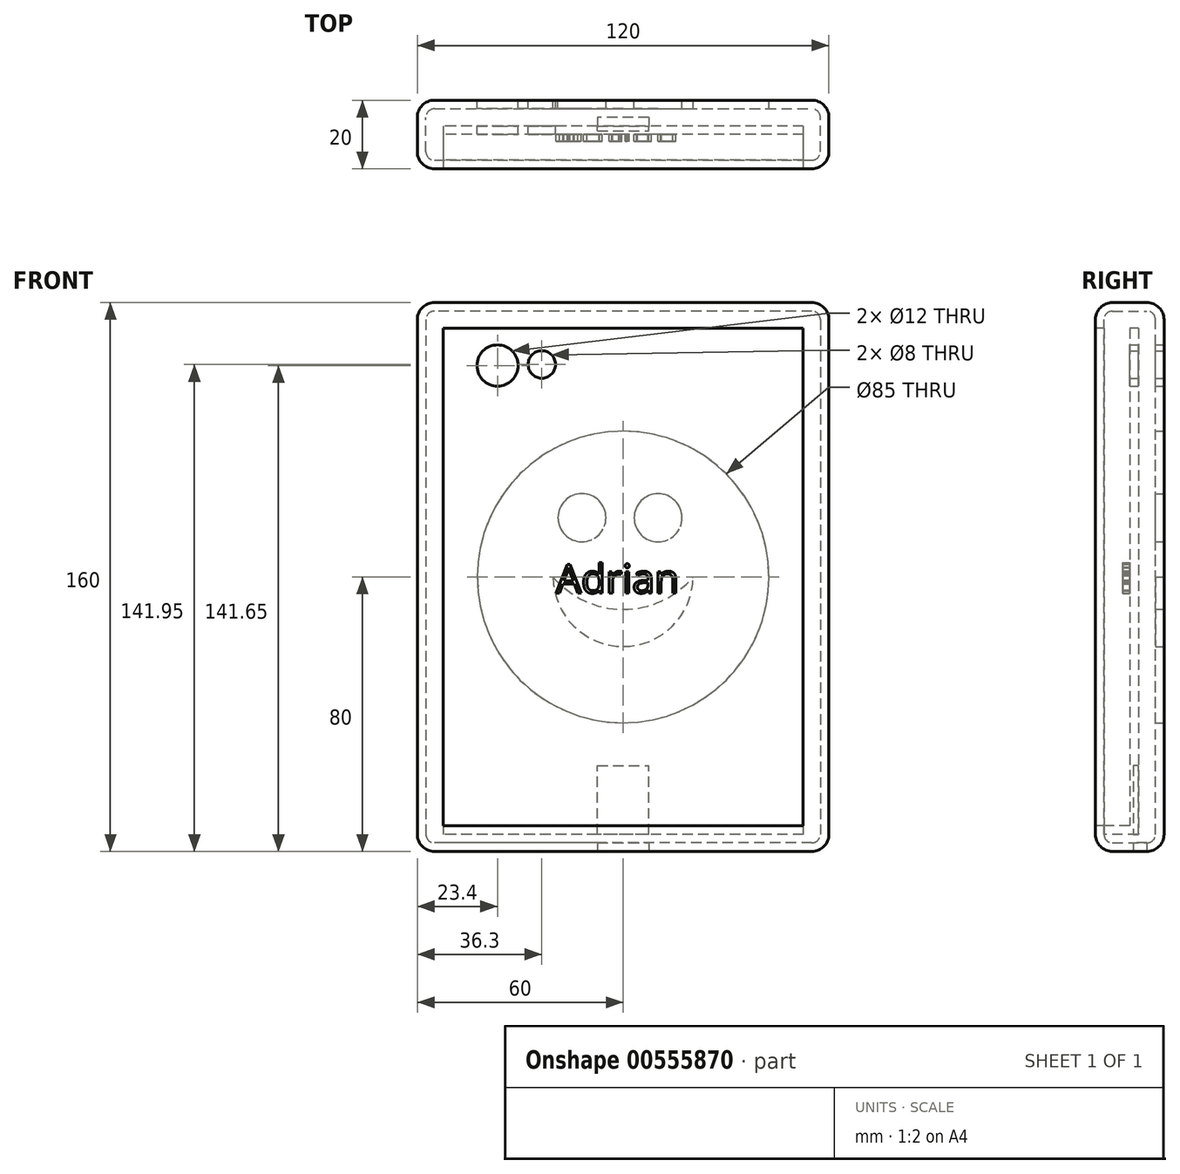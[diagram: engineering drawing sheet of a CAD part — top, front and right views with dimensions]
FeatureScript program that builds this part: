
annotation { "Feature Type Name" : "Feature", "Feature Type Description" : "" }
export const myFeature = defineFeature(function(context is Context, id is Id, definition is map)
    precondition{}
    {
        {
            var Q0;
            Q0=qCreatedBy(makeId("Front.planeOp"),FACE);
            var sketch = newSketch(context, id + "F0", { "sketchPlane" : qUnion([Q0])});
            skLineSegment(sketch, "E0.bottom", {"start": v(60, 80) * mm, "end": v(-60, 80) * mm});
            skLineSegment(sketch, "E0.top", {"start": v(60, -80) * mm, "end": v(-60, -80) * mm});
            skLineSegment(sketch, "E0.left", {"start": v(60, 80) * mm, "end": v(60, -80) * mm});
            skLineSegment(sketch, "E0.right", {"start": v(-60, 80) * mm, "end": v(-60, -80) * mm});
            skPoint(sketch, "E0.middle", {"position": v(0, 0) * mm});
            skSolve(sketch);
        }
        {
            var Q0;
            Q0=makeQuery(id+"F0.imprint","IMPRINT",FACE,{"disambiguationData":[TD([[makeQuery(id+"F0.imprint","IMPRINT",EDGE,{"derivedFrom":sQuery(id+"F0.wireOp",EDGE,"E0.bottom")}),1.0]])]});
            extrude(context, id + "F1", {"entities" : qUnion([Q0]), "depth" : 20 * mm, "offsetDistance" : 25 * mm});
        }
        {
            var Q0;
            Q0=makeQuery(id+"F1.opExtrude","CAP_FACE",FACE,{"disambiguationData":[OSD([sQuery(id+"F0.wireOp",EDGE,"E0.bottom"),sQuery(id+"F0.wireOp",EDGE,"E0.top"),sQuery(id+"F0.wireOp",EDGE,"E0.left"),sQuery(id+"F0.wireOp",EDGE,"E0.right")])],"isStart":false});
            var sketch = newSketch(context, id + "F2", { "sketchPlane" : qUnion([Q0])});
            skLineSegment(sketch, "E1.bottom", {"start": v(52.5, 72.5) * mm, "end": v(-52.5, 72.5) * mm});
            skLineSegment(sketch, "E1.top", {"start": v(52.5, -72.5) * mm, "end": v(-52.5, -72.5) * mm});
            skLineSegment(sketch, "E1.left", {"start": v(52.5, 72.5) * mm, "end": v(52.5, -72.5) * mm});
            skLineSegment(sketch, "E1.right", {"start": v(-52.5, 72.5) * mm, "end": v(-52.5, -72.5) * mm});
            skPoint(sketch, "E1.middle", {"position": v(0, 0) * mm});
            skSolve(sketch);
        }
        {
            var Q0;
            Q0=makeQuery(id+"F2.imprint","IMPRINT",FACE,{"disambiguationData":[TD([[makeQuery(id+"F2.imprint","IMPRINT",EDGE,{"derivedFrom":sQuery(id+"F2.wireOp",EDGE,"E1.bottom")}),1.0]])]});
            extrude(context, id + "F3", {"entities" : qUnion([Q0]), "operationType" : NewBodyOperationType.REMOVE, "oppositeDirection" : true, "depth" : 10 * mm, "offsetDistance" : 25 * mm});
        }
        {
            var Q0;
            Q0=makeQuery(id+"F1.opExtrude","CAP_FACE",FACE,{"disambiguationData":[OSD([sQuery(id+"F0.wireOp",EDGE,"E0.bottom"),sQuery(id+"F0.wireOp",EDGE,"E0.top"),sQuery(id+"F0.wireOp",EDGE,"E0.left"),sQuery(id+"F0.wireOp",EDGE,"E0.right")])],"isStart":true});
            var Q1;
            Q1=makeQuery(id+"F1.opExtrude","SWEPT_FACE",FACE,{"disambiguationData":[OSD([sQuery(id+"F0.wireOp",EDGE,"E0.top")])]});
            var Q2;
            Q2=makeQuery(id+"F1.opExtrude","SWEPT_FACE",FACE,{"disambiguationData":[OSD([sQuery(id+"F0.wireOp",EDGE,"E0.left")])]});
            var Q3;
            Q3=makeQuery(id+"F1.opExtrude","SWEPT_FACE",FACE,{"disambiguationData":[OSD([sQuery(id+"F0.wireOp",EDGE,"E0.bottom")])]});
            var Q4;
            Q4=makeQuery(id+"F1.opExtrude","SWEPT_FACE",FACE,{"disambiguationData":[OSD([sQuery(id+"F0.wireOp",EDGE,"E0.right")])]});
            fillet(context, id + "F4", {"entities" : qUnion([Q0, Q1, Q2, Q3, Q4]), "radius" : 5 * mm, "tangentPropagation" : true, "allowEdgeOverflow" : false});
        }
        {
            var Q0;
            Q0=makeQuery(id+"F3.boolean.opBoolean","COPY",FACE,{"derivedFrom":makeQuery(id+"F3.opExtrude","SWEPT_FACE",FACE,{"disambiguationData":[OSD([sQuery(id+"F2.wireOp",EDGE,"E1.bottom")])]})});
            var Q1;
            Q1=makeQuery(id+"F3.boolean.opBoolean","COPY",FACE,{"derivedFrom":makeQuery(id+"F3.opExtrude","SWEPT_FACE",FACE,{"disambiguationData":[OSD([sQuery(id+"F2.wireOp",EDGE,"E1.right")])]})});
            var Q2;
            Q2=makeQuery(id+"F3.boolean.opBoolean","COPY",FACE,{"derivedFrom":makeQuery(id+"F3.opExtrude","SWEPT_FACE",FACE,{"disambiguationData":[OSD([sQuery(id+"F2.wireOp",EDGE,"E1.left")])]})});
            shell(context, id + "F5", {"entities" : qUnion([Q0, Q1, Q2]), "thickness" : 2.5 * mm});
        }
        {
            var Q0;
            Q0=makeQuery(id+"F1.opExtrude","CAP_FACE",FACE,{"disambiguationData":[OSD([sQuery(id+"F0.wireOp",EDGE,"E0.bottom"),sQuery(id+"F0.wireOp",EDGE,"E0.top"),sQuery(id+"F0.wireOp",EDGE,"E0.left"),sQuery(id+"F0.wireOp",EDGE,"E0.right")])],"isStart":true});
            var sketch = newSketch(context, id + "F6", { "sketchPlane" : qUnion([Q0])});
            skCircle(sketch, "E2", {"center": v(36.6, 61.65) * mm, "radius": 6 * mm});
            skSolve(sketch);
        }
        {
            var Q0;
            Q0=makeQuery(id+"F6.imprint","IMPRINT",FACE,{"disambiguationData":[TD([[makeQuery(id+"F6.imprint","IMPRINT",EDGE,{"derivedFrom":sQuery(id+"F6.wireOp",EDGE,"E2")}),1.0]])]});
            extrude(context, id + "F7", {"entities" : qUnion([Q0]), "operationType" : NewBodyOperationType.REMOVE, "endBound" : BoundingType.THROUGH_ALL, "oppositeDirection" : true, "depth" : 25 * mm, "offsetDistance" : 25 * mm});
        }
        {
            var Q0;
            Q0=makeQuery(id+"F1.opExtrude","CAP_FACE",FACE,{"disambiguationData":[OSD([sQuery(id+"F0.wireOp",EDGE,"E0.bottom"),sQuery(id+"F0.wireOp",EDGE,"E0.top"),sQuery(id+"F0.wireOp",EDGE,"E0.left"),sQuery(id+"F0.wireOp",EDGE,"E0.right")])],"isStart":true});
            var sketch = newSketch(context, id + "F8", { "sketchPlane" : qUnion([Q0])});
            skCircle(sketch, "E3", {"center": v(23.7, 61.95) * mm, "radius": 4 * mm});
            skSolve(sketch);
        }
        {
            var Q0;
            Q0=makeQuery(id+"F8.imprint","IMPRINT",FACE,{"disambiguationData":[TD([[makeQuery(id+"F8.imprint","IMPRINT",EDGE,{"derivedFrom":sQuery(id+"F8.wireOp",EDGE,"E3")}),1.0]])]});
            extrude(context, id + "F9", {"entities" : qUnion([Q0]), "operationType" : NewBodyOperationType.REMOVE, "endBound" : BoundingType.THROUGH_ALL, "oppositeDirection" : true, "depth" : 25 * mm, "offsetDistance" : 25 * mm});
        }
        {
            var Q0;
            Q0=makeQuery(id+"F1.opExtrude","SWEPT_FACE",FACE,{"disambiguationData":[OSD([sQuery(id+"F0.wireOp",EDGE,"E0.top")])]});
            var sketch = newSketch(context, id + "F10", { "sketchPlane" : qUnion([Q0])});
            skLineSegment(sketch, "E4.bottom", {"start": v(-7.5, 5) * mm, "end": v(7.5, 5) * mm});
            skLineSegment(sketch, "E4.top", {"start": v(-7.5, 9) * mm, "end": v(7.5, 9) * mm});
            skLineSegment(sketch, "E4.left", {"start": v(-7.5, 5) * mm, "end": v(-7.5, 9) * mm});
            skLineSegment(sketch, "E4.right", {"start": v(7.5, 5) * mm, "end": v(7.5, 9) * mm});
            skPoint(sketch, "E4.middle", {"position": v(0, 7) * mm});
            skSolve(sketch);
        }
        {
            var Q0;
            Q0=makeQuery(id+"F10.imprint","IMPRINT",FACE,{"disambiguationData":[TD([[makeQuery(id+"F10.imprint","IMPRINT",EDGE,{"derivedFrom":sQuery(id+"F10.wireOp",EDGE,"E4.bottom")}),1.0]])]});
            extrude(context, id + "F11", {"entities" : qUnion([Q0]), "operationType" : NewBodyOperationType.REMOVE, "oppositeDirection" : true, "depth" : 25 * mm, "offsetDistance" : 25 * mm});
        }
        {
            var Q0;
            Q0=makeQuery(id+"F1.opExtrude","CAP_FACE",FACE,{"disambiguationData":[OSD([sQuery(id+"F0.wireOp",EDGE,"E0.bottom"),sQuery(id+"F0.wireOp",EDGE,"E0.top"),sQuery(id+"F0.wireOp",EDGE,"E0.left"),sQuery(id+"F0.wireOp",EDGE,"E0.right")])],"isStart":true});
            var sketch = newSketch(context, id + "F12", { "sketchPlane" : qUnion([Q0])});
            skCircle(sketch, "E5", {"center": v(0, 0) * mm, "radius": 42.5 * mm});
            skArc(sketch, "E6", {"start": v(-20.4, 0) * mm, "mid": v(0, -20.27) * mm, "end": v(20.4, 0) * mm});
            skArc(sketch, "E7", {"start": v(-20.4, 0) * mm, "mid": v(0, -9.45) * mm, "end": v(20.4, 0) * mm});
            skCircle(sketch, "E8", {"center": v(-10.2, 17.25) * mm, "radius": 7 * mm});
            skCircle(sketch, "E9", {"center": v(12, 17.29) * mm, "radius": 7 * mm});
            skSolve(sketch);
        }
        {
            var Q0;
            Q0=makeQuery(id+"F12.imprint","IMPRINT",FACE,{"disambiguationData":[TD([[makeQuery(id+"F12.imprint","IMPRINT",EDGE,{"derivedFrom":sQuery(id+"F12.wireOp",EDGE,"E5")}),1.0]])]});
            extrude(context, id + "F13", {"entities" : qUnion([Q0]), "operationType" : NewBodyOperationType.REMOVE, "oppositeDirection" : true, "depth" : 3 * mm, "offsetDistance" : 25 * mm});
        }
        {
            var Q0;
            {var subQ0=sQuery(id+"F2.wireOp",EDGE,"E1.right");var subQ1=sQuery(id+"F2.wireOp",EDGE,"E1.left");var subQ2=sQuery(id+"F2.wireOp",EDGE,"E1.bottom");var subQ3=sQuery(id+"F2.wireOp",EDGE,"E1.top");Q0=makeQuery(id+"F7.boolean.opBoolean","SPLIT",FACE,{"disambiguationData":[TD([makeQuery(id+"F3.boolean.opBoolean","COPY",FACE,{"derivedFrom":makeQuery(id+"F3.opExtrude","SWEPT_FACE",FACE,{"disambiguationData":[OSD([subQ3])]})}),makeQuery(id+"F5.opShell","OFFSET_FACE",FACE,{"disambiguationData":[OSD([subQ2])]}),makeQuery(id+"F5.opShell","OFFSET_FACE",FACE,{"disambiguationData":[OSD([subQ1])]}),makeQuery(id+"F5.opShell","OFFSET_FACE",FACE,{"disambiguationData":[OSD([subQ0])]}),makeQuery(id+"F7.opExtrude","SWEPT_FACE",FACE,{"disambiguationData":[OSD([sQuery(id+"F6.wireOp",EDGE,"E2")])]})])],"derivedFrom":makeQuery(id+"F3.boolean.opBoolean","COPY",FACE,{"derivedFrom":makeQuery(id+"F3.opExtrude","CAP_FACE",FACE,{"disambiguationData":[OSD([subQ2,subQ3,subQ1,subQ0])],"isStart":false})})});}
            var sketch = newSketch(context, id + "F14", { "sketchPlane" : qUnion([Q0])});
            skText(sketch, "E10", { "text": "Adrian", "fontName": "OpenSans-Regular.ttf"});
            const initialGuessF14  = {"E10": [-0.01958, -0.00468, 1, 0, 0.0084]};
            skSetInitialGuess(sketch, initialGuessF14);
            skSolve(sketch);
        }
        {
            var Q0;
            Q0 = qSketchRegion(id + "F14", true);
            extrude(context, id + "F15", {"entities" : qUnion([Q0]), "operationType" : NewBodyOperationType.ADD, "depth" : 2 * mm, "offsetDistance" : 25 * mm});
        }
    });
